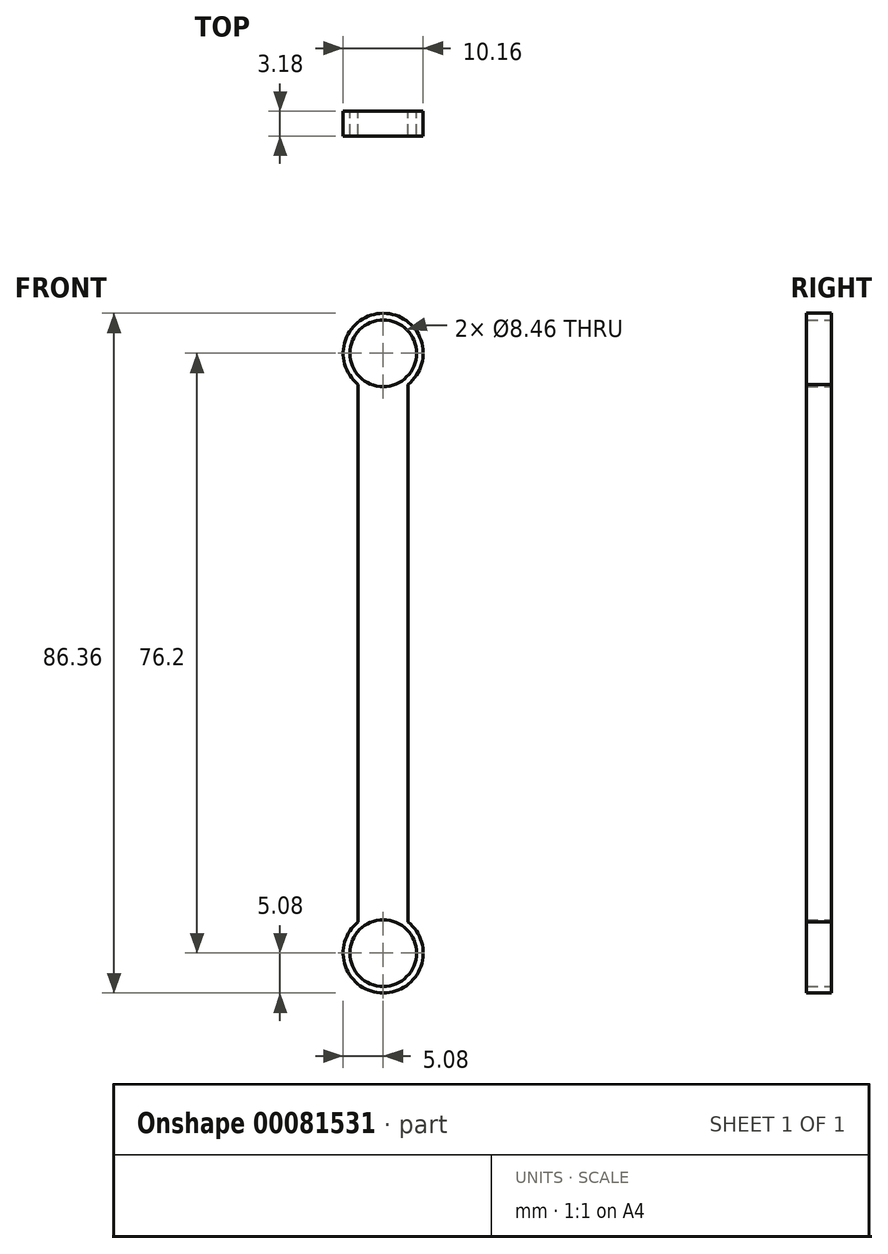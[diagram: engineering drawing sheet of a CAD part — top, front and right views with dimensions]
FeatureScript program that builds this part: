
annotation { "Feature Type Name" : "Feature", "Feature Type Description" : "" }
export const myFeature = defineFeature(function(context is Context, id is Id, definition is map)
    precondition{}
    {
        {
            var Q0;
            Q0=qCreatedBy(makeId("Front.planeOp"),FACE);
            var sketch = newSketch(context, id + "F0", { "sketchPlane" : qUnion([Q0])});
            skLineSegment(sketch, "E0.left", {"start": v(3.18, -34.13) * mm, "end": v(3.18, 34.13) * mm});
            skLineSegment(sketch, "E0.right", {"start": v(-3.17, -34.13) * mm, "end": v(-3.17, 34.13) * mm});
            skPoint(sketch, "E0.middle", {"position": v(0, 0) * mm});
            skPoint(sketch, "E1.orphan", {"position": v(0, 38.1) * mm});
            skPoint(sketch, "E2.end.orphan", {"position": v(0, -38.1) * mm});
            skCircle(sketch, "E3", {"center": v(0, 38.1) * mm, "radius": 5.08 * mm});
            skCircle(sketch, "E4", {"center": v(0, -38.1) * mm, "radius": 5.08 * mm});
            skPoint(sketch, "E5.orphan", {"position": v(-3.17, 38.1) * mm});
            skPoint(sketch, "E6.orphan", {"position": v(3.18, 38.1) * mm});
            skPoint(sketch, "E7.orphan", {"position": v(-3.17, -38.1) * mm});
            skPoint(sketch, "E0.bottom.start.orphan", {"position": v(3.18, -38.1) * mm});
            skCircle(sketch, "E8", {"center": v(0, 38.1) * mm, "radius": 4.23 * mm});
            skCircle(sketch, "E9", {"center": v(0, -38.1) * mm, "radius": 4.23 * mm});
            skPoint(sketch, "E10.end.orphan", {"position": v(3.18, 0) * mm});
            skPoint(sketch, "E11.end.orphan", {"position": v(-3.17, 0) * mm});
            skLineSegment(sketch, "E12", {"start": v(-3.17, 0) * mm, "end": v(3.18, 0) * mm});
            skSolve(sketch);
        }
        {
            var Q0;
            Q0 = qSketchRegion(id + "F0", true);
            extrude(context, id + "F1", {"entities" : qUnion([Q0]), "depth" : 3.17 * mm});
        }
    });
